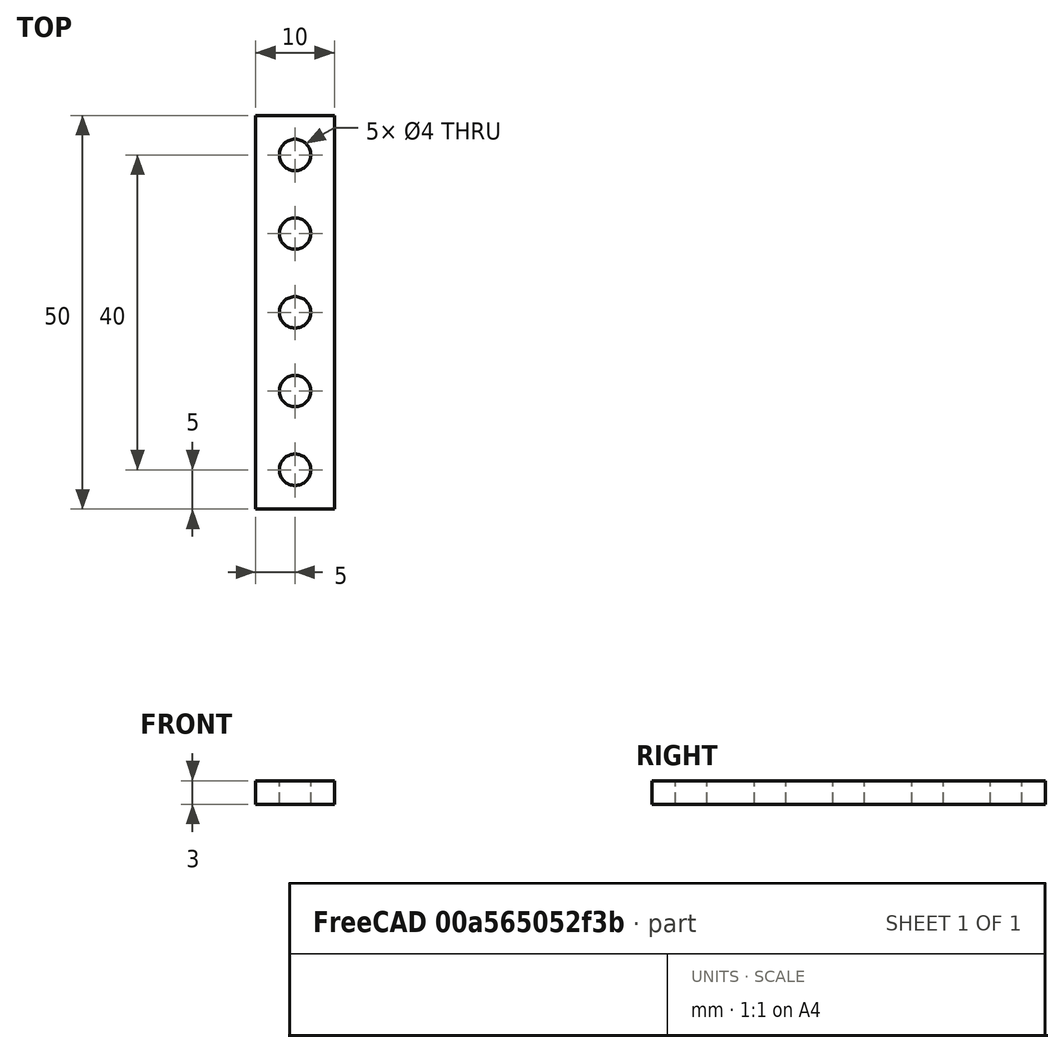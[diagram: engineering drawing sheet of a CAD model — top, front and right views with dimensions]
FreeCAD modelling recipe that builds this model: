
FCSTD DOCUMENT  (FreeCAD 0.17R13217 (Git))
Label: 05-pieza-mecano
License: All rights reserved
LicenseURL: http://en.wikipedia.org/wiki/All_rights_reserved
objects: Part::Cylinder×5, Part::Box×1, Part::MultiFuse×1, Part::Cut×1
note: 8 computed .brp shape members not serialized (recipe doc carries the construction recipe); baked Part::Feature solids carry a one-line shape summary decoded from their .brp

FEATURE [Part::Box] Box  label="base"
  AttacherType = Attacher::AttachEngine3D
  Height = 3
  Length = 10
  Width = 50
FEATURE [Part::Cylinder] Cylinder  label="Cilindro"
  Angle = 360
  AttacherType = Attacher::AttachEngine3D
  Height = 10
  Placement = pos=(5,5,-3) rot=(0,0,1;0rad)
  Radius = 2
FEATURE [Part::Cylinder] Cylinder001  label="Cilindro001"
  Angle = 360
  AttacherType = Attacher::AttachEngine3D
  Height = 10
  Placement = pos=(5,15,-3) rot=(0,0,1;0rad)
  Radius = 2
FEATURE [Part::Cylinder] Cylinder002  label="Cilindro002"
  Angle = 360
  AttacherType = Attacher::AttachEngine3D
  Height = 10
  Placement = pos=(5,25,-3) rot=(0,0,1;0rad)
  Radius = 2
FEATURE [Part::Cylinder] Cylinder003  label="Cilindro003"
  Angle = 360
  AttacherType = Attacher::AttachEngine3D
  Height = 10
  Placement = pos=(5,35,-3) rot=(0,0,1;0rad)
  Radius = 2
FEATURE [Part::Cylinder] Cylinder004  label="Cilindro004"
  Angle = 360
  AttacherType = Attacher::AttachEngine3D
  Height = 10
  Placement = pos=(5,45,-3) rot=(0,0,1;0rad)
  Radius = 2
FEATURE [Part::MultiFuse] Fusion
  Refine = true
  Shapes = -> [Cylinder,Cylinder003,Cylinder002,Cylinder004,Cylinder001]
FEATURE [Part::Cut] Cut
  Base = -> Box
  Refine = true
  Tool = -> Fusion
